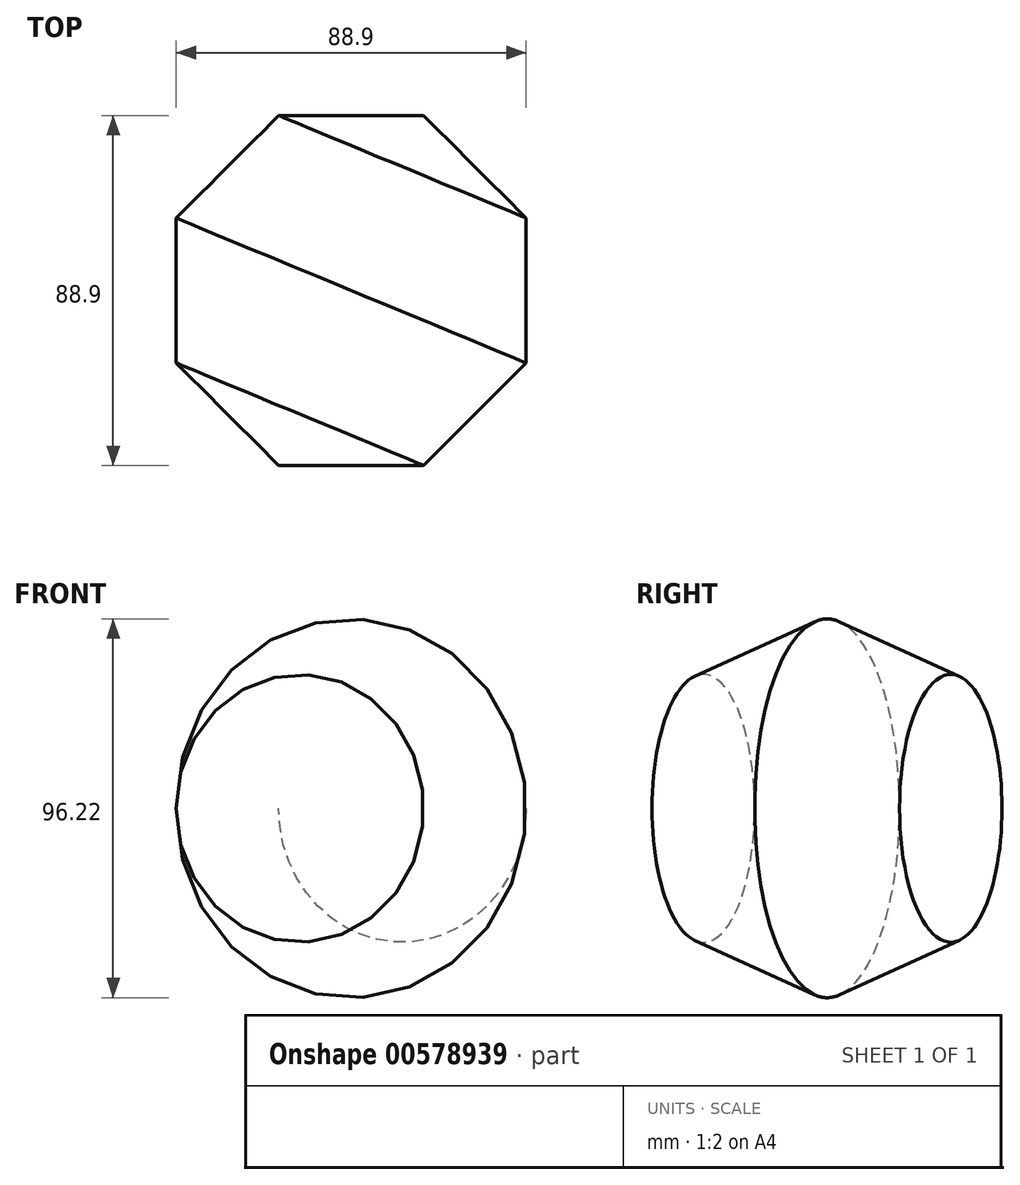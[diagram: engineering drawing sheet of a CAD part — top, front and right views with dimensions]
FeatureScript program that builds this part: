
annotation { "Feature Type Name" : "Feature", "Feature Type Description" : "" }
export const myFeature = defineFeature(function(context is Context, id is Id, definition is map)
    precondition{}
    {
        {
            var Q0;
            Q0=qCreatedBy(makeId("Top.planeOp"),FACE);
            var sketch = newSketch(context, id + "F0", { "sketchPlane" : qUnion([Q0])});
            skCircle(sketch, "E0.cCircle", {"center": v(0, 0) * mm, "radius": 44.45 * mm, "construction": true});
            skLineSegment(sketch, "E0.0", {"start": v(18.41, -44.45) * mm, "end": v(-18.41, -44.45) * mm});
            skLineSegment(sketch, "E0.1", {"start": v(-18.41, -44.45) * mm, "end": v(-44.45, -18.41) * mm});
            skLineSegment(sketch, "E0.2", {"start": v(-44.45, -18.41) * mm, "end": v(-44.45, 18.41) * mm});
            skLineSegment(sketch, "E0.3", {"start": v(-44.45, 18.41) * mm, "end": v(-18.41, 44.45) * mm});
            skLineSegment(sketch, "E0.4", {"start": v(-18.41, 44.45) * mm, "end": v(18.41, 44.45) * mm});
            skLineSegment(sketch, "E0.5", {"start": v(18.41, 44.45) * mm, "end": v(44.45, 18.41) * mm});
            skLineSegment(sketch, "E0.6", {"start": v(44.45, 18.41) * mm, "end": v(44.45, -18.41) * mm});
            skLineSegment(sketch, "E0.7", {"start": v(44.45, -18.41) * mm, "end": v(18.41, -44.45) * mm});
            skPoint(sketch, "E0.0.midPoint", {"position": v(0, -44.45) * mm});
            skLineSegment(sketch, "E1", {"start": v(-44.45, -18.41) * mm, "end": v(18.41, 44.45) * mm, "construction": true});
            skLineSegment(sketch, "E2", {"start": v(18.41, -44.45) * mm, "end": v(18.41, 44.45) * mm, "construction": true});
            skLineSegment(sketch, "E3", {"start": v(18.41, 44.45) * mm, "end": v(-44.45, 18.41) * mm});
            skLineSegment(sketch, "E4", {"start": v(18.41, 44.45) * mm, "end": v(-18.41, -44.45) * mm});
            skLineSegment(sketch, "E5", {"start": v(18.41, 40.46) * mm, "end": v(44.45, -18.41) * mm});
            skSolve(sketch);
        }
        {
            var Q0;
            Q0=makeQuery(id+"F0.imprint","IMPRINT",FACE,{"disambiguationData":[TD([[makeQuery(id+"F0.imprint","IMPRINT",EDGE,{"derivedFrom":sQuery(id+"F0.wireOp",EDGE,"E0.3")}),-1.0]])]});
            var Q1;
            Q1=makeQuery(id+"F0.imprint","IMPRINT",FACE,{"disambiguationData":[TD([[makeQuery(id+"F0.imprint","IMPRINT",EDGE,{"derivedFrom":sQuery(id+"F0.wireOp",EDGE,"E0.1")}),-1.0]])]});
            var Q2;
            Q2=sQuery(id+"F0.wireOp",EDGE,"E4");
            revolve(context, id + "F1", {"surfaceOperationType" : NewSurfaceOperationType.NEW, "entities" : qUnion([Q0, Q1]), "axis" : qUnion([Q2]), "revolveType" : RevolveType.FULL});
        }
    });
